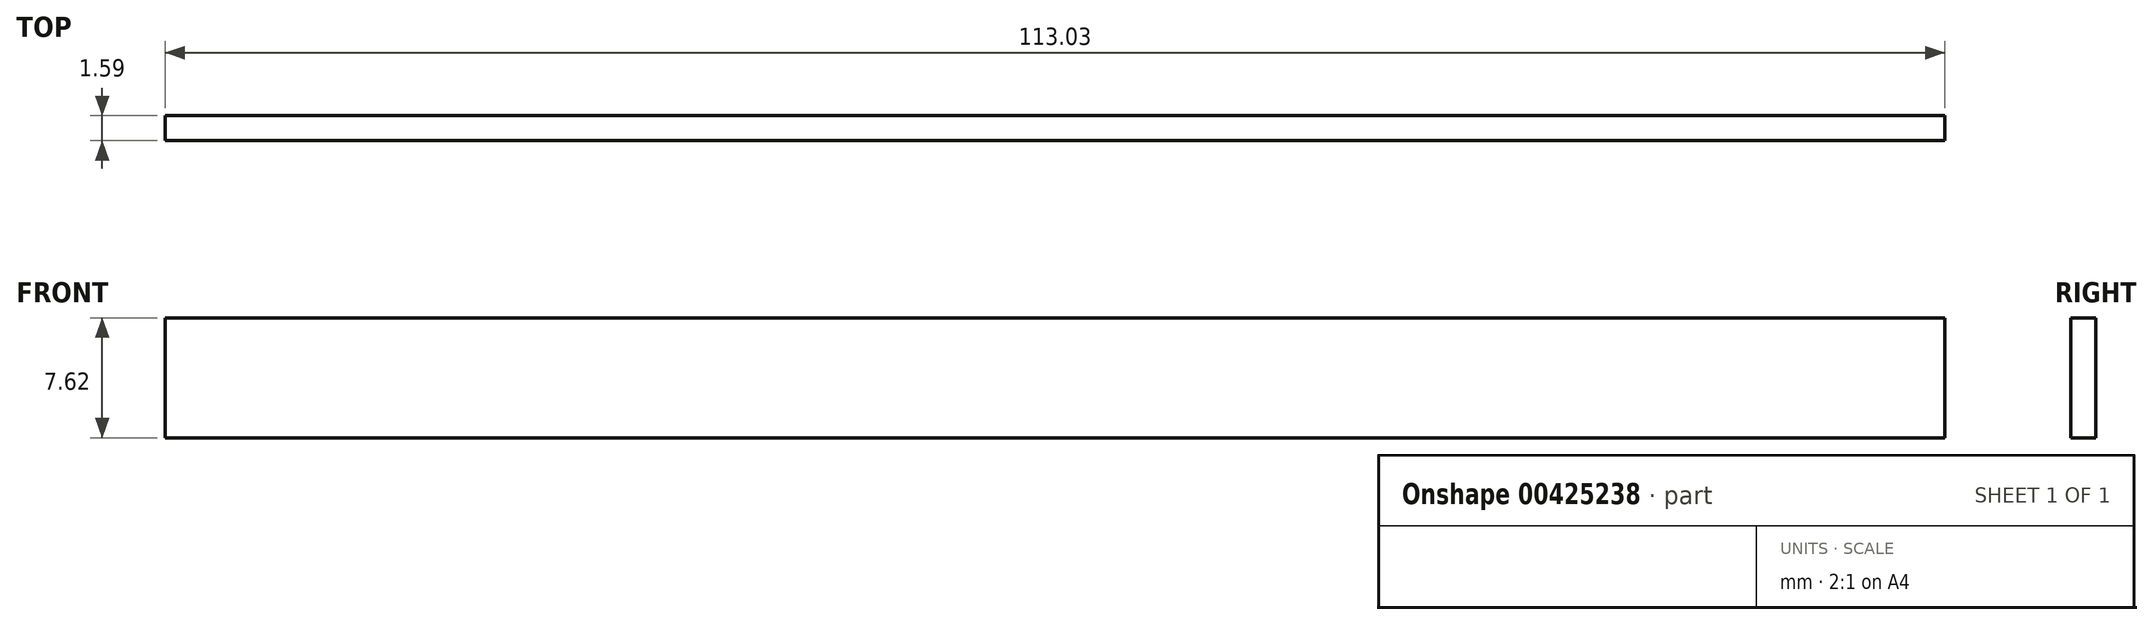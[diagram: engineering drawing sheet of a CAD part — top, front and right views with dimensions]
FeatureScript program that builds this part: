
annotation { "Feature Type Name" : "Feature", "Feature Type Description" : "" }
export const myFeature = defineFeature(function(context is Context, id is Id, definition is map)
    precondition{}
    {
        {
            var Q0;
            Q0=qCreatedBy(makeId("Front.planeOp"),FACE);
            var sketch = newSketch(context, id + "F0", { "sketchPlane" : qUnion([Q0])});
            skLineSegment(sketch, "E0.bottom", {"start": v(-48.84, 28.24) * mm, "end": v(64.19, 28.24) * mm});
            skLineSegment(sketch, "E0.top", {"start": v(-48.84, 20.62) * mm, "end": v(64.19, 20.62) * mm});
            skLineSegment(sketch, "E0.left", {"start": v(-48.84, 28.24) * mm, "end": v(-48.84, 20.62) * mm});
            skLineSegment(sketch, "E0.right", {"start": v(64.19, 28.24) * mm, "end": v(64.19, 20.62) * mm});
            skSolve(sketch);
        }
        {
            var Q0;
            Q0=makeQuery(id+"F0.imprint","IMPRINT",FACE,{"disambiguationData":[TD([[makeQuery(id+"F0.imprint","IMPRINT",EDGE,{"derivedFrom":sQuery(id+"F0.wireOp",EDGE,"E0.bottom")}),-1.0]])]});
            extrude(context, id + "F1", {"entities" : qUnion([Q0]), "depth" : 1.59 * mm});
        }
    });
